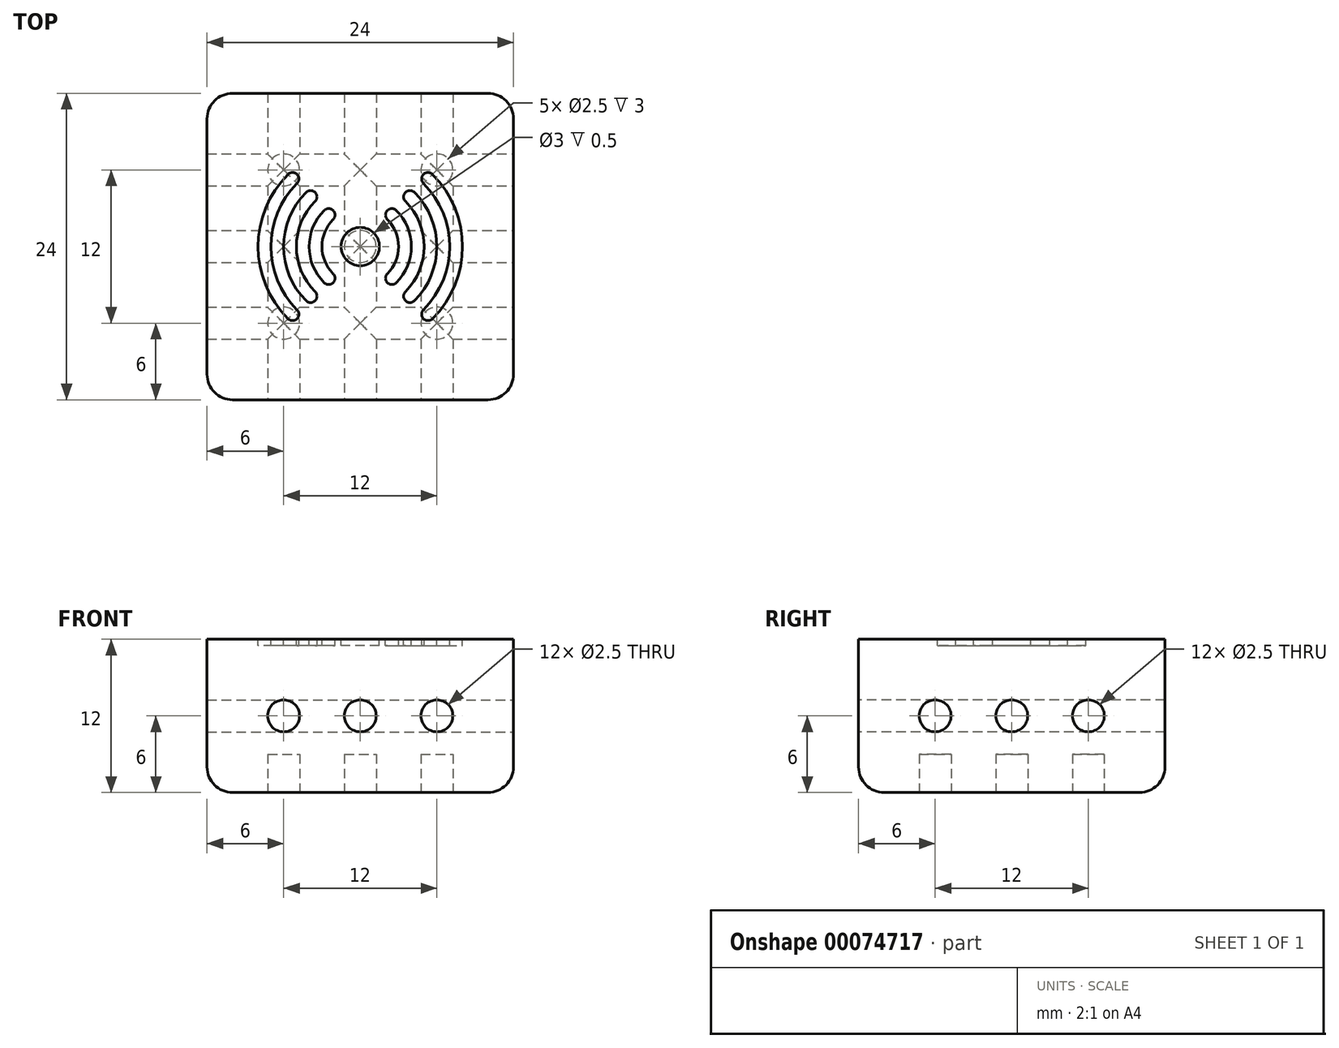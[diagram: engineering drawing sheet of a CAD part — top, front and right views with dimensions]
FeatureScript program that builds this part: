
annotation { "Feature Type Name" : "Feature", "Feature Type Description" : "" }
export const myFeature = defineFeature(function(context is Context, id is Id, definition is map)
    precondition{}
    {
        {
            var Q0;
            Q0=qCreatedBy(makeId("Right.planeOp"),FACE);
            var sketch = newSketch(context, id + "F0", { "sketchPlane" : qUnion([Q0])});
            skLineSegment(sketch, "E0.rect.bottom", {"start": v(12, -6) * mm, "end": v(-12, -6) * mm});
            skLineSegment(sketch, "E0.rect.top", {"start": v(12, 6) * mm, "end": v(-12, 6) * mm});
            skLineSegment(sketch, "E0.rect.left", {"start": v(12, -6) * mm, "end": v(12, 6) * mm});
            skLineSegment(sketch, "E0.rect.right", {"start": v(-12, -6) * mm, "end": v(-12, 6) * mm});
            skPoint(sketch, "E0.rect.middle", {"position": v(0, 0) * mm});
            skSolve(sketch);
        }
        {
            var Q0;
            Q0=makeQuery(id+"F0.imprint","IMPRINT",FACE,{"disambiguationData":[TD([[makeQuery(id+"F0.imprint","IMPRINT",EDGE,{"derivedFrom":sQuery(id+"F0.wireOp",EDGE,"E0.rect.bottom")}),-1.0]])]});
            extrude(context, id + "F1", {"entities" : qUnion([Q0]), "endBound" : BoundingType.SYMMETRIC, "depth" : 24 * mm});
        }
        {
            var Q0;
            Q0=makeQuery(id+"F1.opExtrude","CAP_FACE",FACE,{"disambiguationData":[OSD([sQuery(id+"F0.wireOp",EDGE,"E0.rect.bottom"),sQuery(id+"F0.wireOp",EDGE,"E0.rect.top"),sQuery(id+"F0.wireOp",EDGE,"E0.rect.left"),sQuery(id+"F0.wireOp",EDGE,"E0.rect.right")])],"isStart":false});
            var sketch = newSketch(context, id + "F2", { "sketchPlane" : qUnion([Q0])});
            skLineSegment(sketch, "E1", {"start": v(-6, 0) * mm, "end": v(6, 0) * mm, "construction": true});
            skCircle(sketch, "E2", {"center": v(-6, 0) * mm, "radius": 1.25 * mm});
            skCircle(sketch, "E3", {"center": v(0, 0) * mm, "radius": 1.25 * mm});
            skCircle(sketch, "E4", {"center": v(6, 0) * mm, "radius": 1.25 * mm});
            skSolve(sketch);
        }
        {
            var Q0;
            Q0=makeQuery(id+"F1.opExtrude","SWEPT_FACE",FACE,{"disambiguationData":[OSD([sQuery(id+"F0.wireOp",EDGE,"E0.rect.right")])]});
            var sketch = newSketch(context, id + "F3", { "sketchPlane" : qUnion([Q0])});
            skLineSegment(sketch, "E5", {"start": v(-6, 0) * mm, "end": v(6, 0) * mm, "construction": true});
            skCircle(sketch, "E6", {"center": v(-6, 0) * mm, "radius": 1.25 * mm});
            skCircle(sketch, "E7", {"center": v(0, 0) * mm, "radius": 1.25 * mm});
            skCircle(sketch, "E8", {"center": v(6, 0) * mm, "radius": 1.25 * mm});
            skSolve(sketch);
        }
        {
            var Q0;
            Q0=makeQuery(id+"F1.opExtrude","SWEPT_FACE",FACE,{"disambiguationData":[OSD([sQuery(id+"F0.wireOp",EDGE,"E0.rect.bottom")])]});
            var sketch = newSketch(context, id + "F4", { "sketchPlane" : qUnion([Q0])});
            skLineSegment(sketch, "E9.0", {"start": v(-6, 6) * mm, "end": v(-6, -6) * mm, "construction": true});
            skLineSegment(sketch, "E9.1", {"start": v(6, 6) * mm, "end": v(-6, 6) * mm, "construction": true});
            skLineSegment(sketch, "E9.2", {"start": v(6, -6) * mm, "end": v(6, 6) * mm, "construction": true});
            skLineSegment(sketch, "E9.3", {"start": v(-6, -6) * mm, "end": v(6, -6) * mm, "construction": true});
            skCircle(sketch, "E10", {"center": v(-6, 6) * mm, "radius": 1.25 * mm});
            skCircle(sketch, "E11", {"center": v(6, 6) * mm, "radius": 1.25 * mm});
            skCircle(sketch, "E12", {"center": v(6, -6) * mm, "radius": 1.25 * mm});
            skCircle(sketch, "E13", {"center": v(0, 0) * mm, "radius": 1.25 * mm});
            skCircle(sketch, "E14", {"center": v(-6, -6) * mm, "radius": 1.25 * mm});
            skSolve(sketch);
        }
        {
            var Q0;
            Q0=makeQuery(id+"F1.opExtrude","SWEPT_FACE",FACE,{"disambiguationData":[OSD([sQuery(id+"F0.wireOp",EDGE,"E0.rect.top")])]});
            var sketch = newSketch(context, id + "F5", { "sketchPlane" : qUnion([Q0])});
            skArc(sketch, "E15", {"start": v(-2.47, 2.47) * mm, "mid": v(-3.5, 0) * mm, "end": v(-2.47, -2.47) * mm});
            skArc(sketch, "E16", {"start": v(-3.89, 3.89) * mm, "mid": v(-5.5, 0) * mm, "end": v(-3.89, -3.89) * mm});
            skArc(sketch, "E17", {"start": v(-5.3, 5.3) * mm, "mid": v(-7.5, 0) * mm, "end": v(-5.3, -5.3) * mm});
            skLineSegment(sketch, "E18", {"start": v(-5.3, 5.3) * mm, "end": v(5.3, -5.3) * mm, "construction": true});
            skLineSegment(sketch, "E19", {"start": v(-5.3, -5.3) * mm, "end": v(5.3, 5.3) * mm, "construction": true});
            skLineSegment(sketch, "E20", {"start": v(-9.5, 0) * mm, "end": v(9.83, 0) * mm, "construction": true});
            skCircle(sketch, "E21", {"center": v(0, 0) * mm, "radius": 1.5 * mm});
            skArc(sketch, "E22.trimOffspring", {"start": v(2.47, -2.47) * mm, "mid": v(3.5, 0) * mm, "end": v(2.47, 2.47) * mm});
            skArc(sketch, "E23.trimOffspring", {"start": v(3.89, -3.89) * mm, "mid": v(5.5, 0) * mm, "end": v(3.89, 3.89) * mm});
            skArc(sketch, "E24.trimOffspring", {"start": v(5.3, -5.3) * mm, "mid": v(7.5, 0) * mm, "end": v(5.3, 5.3) * mm});
            skArc(sketch, "E25.0.startCap", {"start": v(-5.66, 5.66) * mm, "mid": v(-4.95, 5.66) * mm, "end": v(-4.95, 4.95) * mm});
            skArc(sketch, "E25.0.endCap", {"start": v(-4.95, -4.95) * mm, "mid": v(-4.95, -5.66) * mm, "end": v(-5.66, -5.66) * mm});
            skArc(sketch, "E25.0.left", {"start": v(-4.95, 4.95) * mm, "mid": v(-7, 0) * mm, "end": v(-4.95, -4.95) * mm});
            skArc(sketch, "E25.0.right", {"start": v(-5.66, 5.66) * mm, "mid": v(-8, 0) * mm, "end": v(-5.66, -5.66) * mm});
            skArc(sketch, "E26.0.startCap", {"start": v(-4.24, 4.24) * mm, "mid": v(-3.54, 4.24) * mm, "end": v(-3.54, 3.54) * mm});
            skArc(sketch, "E26.0.endCap", {"start": v(-3.54, -3.54) * mm, "mid": v(-3.54, -4.24) * mm, "end": v(-4.24, -4.24) * mm});
            skArc(sketch, "E26.0.left", {"start": v(-3.54, 3.54) * mm, "mid": v(-5, 0) * mm, "end": v(-3.54, -3.54) * mm});
            skArc(sketch, "E26.0.right", {"start": v(-4.24, 4.24) * mm, "mid": v(-6, 0) * mm, "end": v(-4.24, -4.24) * mm});
            skArc(sketch, "E27.0.startCap", {"start": v(-2.83, 2.83) * mm, "mid": v(-2.12, 2.83) * mm, "end": v(-2.12, 2.12) * mm});
            skArc(sketch, "E27.0.endCap", {"start": v(-2.12, -2.12) * mm, "mid": v(-2.12, -2.83) * mm, "end": v(-2.83, -2.83) * mm});
            skArc(sketch, "E27.0.left", {"start": v(-2.12, 2.12) * mm, "mid": v(-3, 0) * mm, "end": v(-2.12, -2.12) * mm});
            skArc(sketch, "E27.0.right", {"start": v(-2.83, 2.83) * mm, "mid": v(-4, 0) * mm, "end": v(-2.83, -2.83) * mm});
            skArc(sketch, "E28.0.startCap", {"start": v(2.83, -2.83) * mm, "mid": v(2.12, -2.83) * mm, "end": v(2.12, -2.12) * mm});
            skArc(sketch, "E28.0.endCap", {"start": v(2.12, 2.12) * mm, "mid": v(2.12, 2.83) * mm, "end": v(2.83, 2.83) * mm});
            skArc(sketch, "E28.0.left", {"start": v(2.12, -2.12) * mm, "mid": v(3, 0) * mm, "end": v(2.12, 2.12) * mm});
            skArc(sketch, "E28.0.right", {"start": v(2.83, -2.83) * mm, "mid": v(4, 0) * mm, "end": v(2.83, 2.83) * mm});
            skArc(sketch, "E29.0.startCap", {"start": v(4.24, -4.24) * mm, "mid": v(3.54, -4.24) * mm, "end": v(3.54, -3.54) * mm});
            skArc(sketch, "E29.0.endCap", {"start": v(3.54, 3.54) * mm, "mid": v(3.54, 4.24) * mm, "end": v(4.24, 4.24) * mm});
            skArc(sketch, "E29.0.left", {"start": v(3.54, -3.54) * mm, "mid": v(5, 0) * mm, "end": v(3.54, 3.54) * mm});
            skArc(sketch, "E29.0.right", {"start": v(4.24, -4.24) * mm, "mid": v(6, 0) * mm, "end": v(4.24, 4.24) * mm});
            skArc(sketch, "E30.0.startCap", {"start": v(5.66, -5.66) * mm, "mid": v(4.95, -5.66) * mm, "end": v(4.95, -4.95) * mm});
            skArc(sketch, "E30.0.endCap", {"start": v(4.95, 4.95) * mm, "mid": v(4.95, 5.66) * mm, "end": v(5.66, 5.66) * mm});
            skArc(sketch, "E30.0.left", {"start": v(4.95, -4.95) * mm, "mid": v(7, 0) * mm, "end": v(4.95, 4.95) * mm});
            skArc(sketch, "E30.0.right", {"start": v(5.66, -5.66) * mm, "mid": v(8, 0) * mm, "end": v(5.66, 5.66) * mm});
            skSolve(sketch);
        }
        {
            var Q0;
            Q0=makeQuery(id+"F1.opExtrude","SWEPT_FACE",FACE,{"disambiguationData":[OSD([sQuery(id+"F0.wireOp",EDGE,"E0.rect.bottom")])]});
            var Q1;
            Q1=makeQuery(id+"F1.opExtrude","CAP_EDGE",EDGE,{"disambiguationData":[OSD([sQuery(id+"F0.wireOp",EDGE,"E0.rect.right")])],"isStart":false});
            var Q2;
            Q2=makeQuery(id+"F1.opExtrude","CAP_EDGE",EDGE,{"disambiguationData":[OSD([sQuery(id+"F0.wireOp",EDGE,"E0.rect.right")])],"isStart":true});
            var Q3;
            Q3=makeQuery(id+"F1.opExtrude","CAP_EDGE",EDGE,{"disambiguationData":[OSD([sQuery(id+"F0.wireOp",EDGE,"E0.rect.left")])],"isStart":false});
            var Q4;
            Q4=makeQuery(id+"F1.opExtrude","CAP_EDGE",EDGE,{"disambiguationData":[OSD([sQuery(id+"F0.wireOp",EDGE,"E0.rect.left")])],"isStart":true});
            fillet(context, id + "F6", {"entities" : qUnion([Q0, Q1, Q2, Q3, Q4]), "radius" : 2 * mm, "tangentPropagation" : true, "allowEdgeOverflow" : false});
        }
        {
            var Q0;
            Q0=qSketchRegion(id+"F2",true);
            extrude(context, id + "F7", {"entities" : qUnion([Q0]), "operationType" : NewBodyOperationType.REMOVE, "endBound" : BoundingType.THROUGH_ALL, "oppositeDirection" : true, "depth" : 25 * mm});
        }
        {
            var Q0;
            Q0=qSketchRegion(id+"F3",true);
            extrude(context, id + "F8", {"entities" : qUnion([Q0]), "operationType" : NewBodyOperationType.REMOVE, "endBound" : BoundingType.THROUGH_ALL, "oppositeDirection" : true, "depth" : 25 * mm});
        }
        {
            var Q0;
            Q0=qSketchRegion(id+"F4",true);
            extrude(context, id + "F9", {"entities" : qUnion([Q0]), "operationType" : NewBodyOperationType.REMOVE, "oppositeDirection" : true, "depth" : 3 * mm});
        }
        {
            var Q0;
            Q0=qSketchRegion(id+"F5",true);
            extrude(context, id + "F10", {"entities" : qUnion([Q0]), "operationType" : NewBodyOperationType.REMOVE, "oppositeDirection" : true, "depth" : 0.5 * mm});
        }
    });
